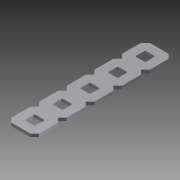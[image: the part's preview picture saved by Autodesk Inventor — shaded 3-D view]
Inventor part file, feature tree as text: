
AUTODESK INVENTOR PART (.ipt)
format: ipt  version: 2014 SP1 (Build 180222100, 222)  size: 485,888 bytes
history: native  units: in
note: dims shown in document units (in); Inventor stores cm internally (conversion verified against a paired STEP export)
features: other x1, imported_body x1, extrude x1, sketch x1
ambient origin geometry x8: Origin, YZ Plane, XZ Plane, XY Plane, X Axis, Y Axis, Z Axis, Center Point
bodies: Body1 (feature_tree)
feature tree (4):
  parser-record x1  (decoder bookkeeping rows leaked as tree rows — omitted from the tree; the rows remain in map.json)
  imported_body  "Base1"
  extrude  "Extrusion1"  Depth=1.0in TaperAngle=0.0deg
  sketch  "Sketch1"  dims[d0=2.5in d1=1.0in d2=0.0in]
